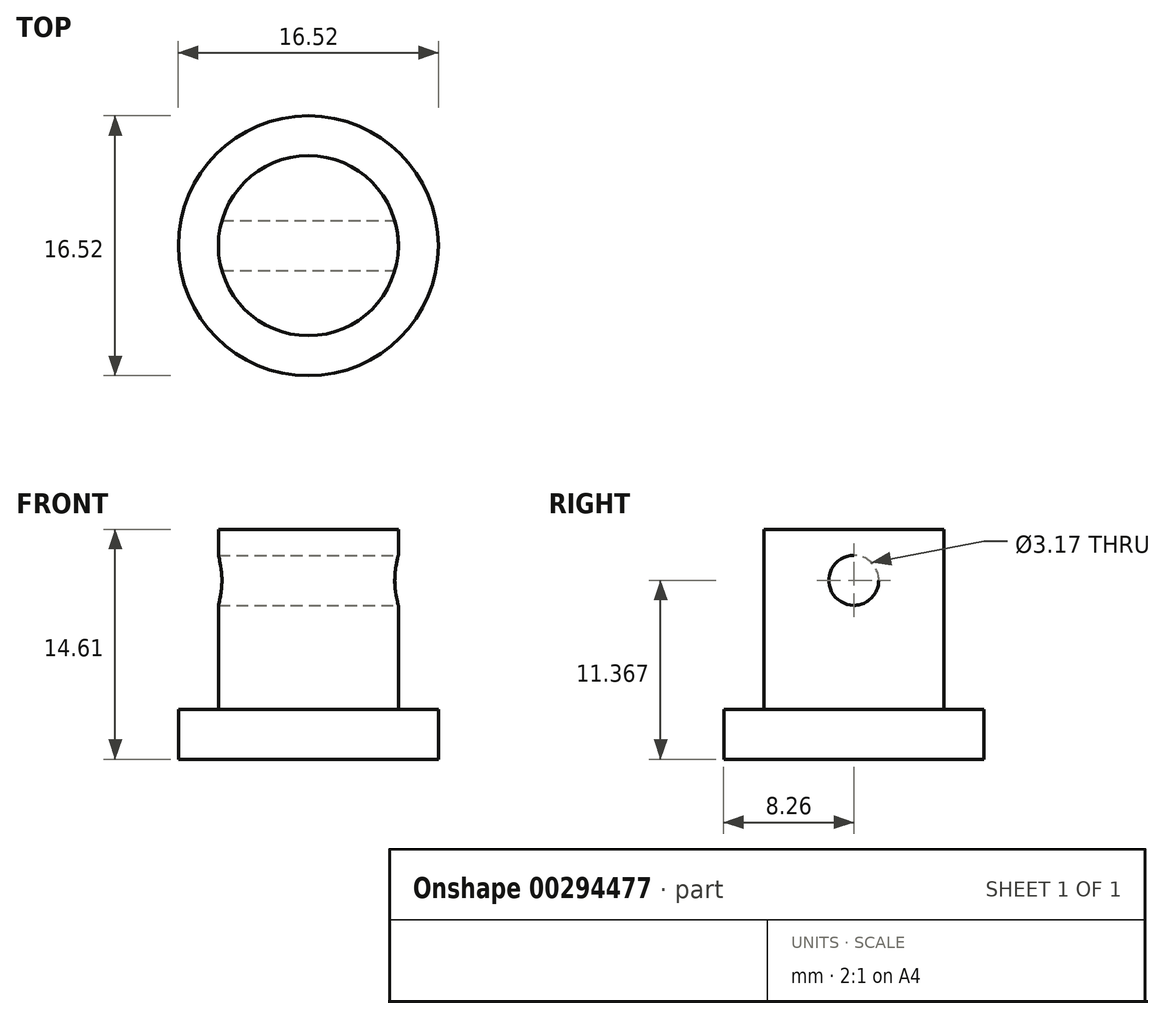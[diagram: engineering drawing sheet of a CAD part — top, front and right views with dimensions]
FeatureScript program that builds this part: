
annotation { "Feature Type Name" : "Feature", "Feature Type Description" : "" }
export const myFeature = defineFeature(function(context is Context, id is Id, definition is map)
    precondition{}
    {
        {
            var Q0;
            Q0=qCreatedBy(makeId("Top.planeOp"),FACE);
            var sketch = newSketch(context, id + "F0", { "sketchPlane" : qUnion([Q0])});
            skCircle(sketch, "E0", {"center": v(0, 0) * mm, "radius": 8.26 * mm});
            skSolve(sketch);
        }
        {
            var Q0;
            Q0=makeQuery(id+"F0.imprint","IMPRINT",FACE,{"disambiguationData":[TD([[makeQuery(id+"F0.imprint","IMPRINT",EDGE,{"derivedFrom":sQuery(id+"F0.wireOp",EDGE,"E0")}),1.0]])]});
            extrude(context, id + "F1", {"entities" : qUnion([Q0]), "depth" : 3.17 * mm});
        }
        {
            var Q0;
            Q0=makeQuery(id+"F1.opExtrude","CAP_FACE",FACE,{"disambiguationData":[OSD([sQuery(id+"F0.wireOp",EDGE,"E0")])],"isStart":false});
            var sketch = newSketch(context, id + "F2", { "sketchPlane" : qUnion([Q0])});
            skCircle(sketch, "E1", {"center": v(0, 0) * mm, "radius": 5.71 * mm});
            skSolve(sketch);
        }
        {
            var Q0;
            Q0 = qSketchRegion(id + "F2", true);
            extrude(context, id + "F3", {"entities" : qUnion([Q0]), "operationType" : NewBodyOperationType.ADD, "depth" : 11.43 * mm});
        }
        {
            var Q0;
            Q0=qCreatedBy(makeId("Right.planeOp"),FACE);
            var sketch = newSketch(context, id + "F4", { "sketchPlane" : qUnion([Q0])});
            skLineSegment(sketch, "E2.bottom", {"start": v(2.54, 9.78) * mm, "end": v(-2.54, 9.78) * mm, "construction": true});
            skLineSegment(sketch, "E2.top", {"start": v(2.54, 11.05) * mm, "end": v(-2.54, 11.05) * mm, "construction": true});
            skLineSegment(sketch, "E2.left", {"start": v(2.54, 9.78) * mm, "end": v(2.54, 11.05) * mm, "construction": true});
            skLineSegment(sketch, "E2.right", {"start": v(-2.54, 9.78) * mm, "end": v(-2.54, 11.05) * mm, "construction": true});
            skPoint(sketch, "E2.middle", {"position": v(0, 10.41) * mm});
            skCircle(sketch, "E3", {"center": v(0, 11.37) * mm, "radius": 1.59 * mm});
            skPoint(sketch, "E3.centerSnap0", {"position": v(0, 9.78) * mm});
            skSolve(sketch);
        }
        {
            var Q0;
            Q0 = qSketchRegion(id + "F4", true);
            extrude(context, id + "F5", {"entities" : qUnion([Q0]), "operationType" : NewBodyOperationType.REMOVE, "endBound" : BoundingType.THROUGH_ALL, "oppositeDirection" : true, "depth" : 25.4 * mm, "hasSecondDirection" : true, "secondDirectionOppositeDirection" : false, "secondDirectionDepth" : 25.4 * mm});
        }
    });
